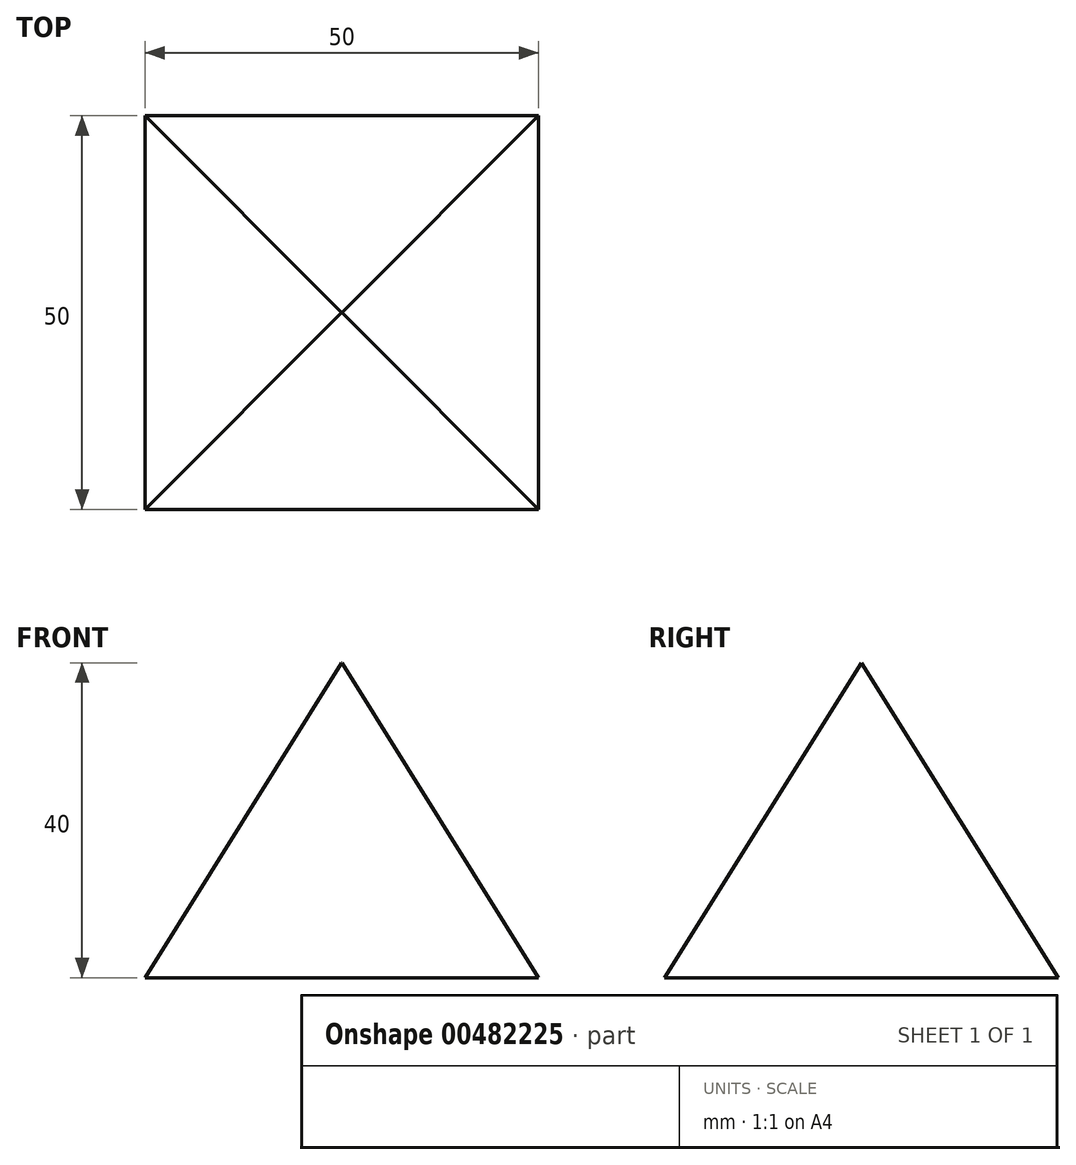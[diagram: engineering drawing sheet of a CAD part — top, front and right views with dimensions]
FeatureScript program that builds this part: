
annotation { "Feature Type Name" : "Feature", "Feature Type Description" : "" }
export const myFeature = defineFeature(function(context is Context, id is Id, definition is map)
    precondition{}
    {
        {
            var Q0;
            Q0=qCreatedBy(makeId("Top.planeOp"),FACE);
            var sketch = newSketch(context, id + "F0", { "sketchPlane" : qUnion([Q0])});
            skLineSegment(sketch, "E0.bottom", {"start": v(25, 25) * mm, "end": v(-25, 25) * mm});
            skLineSegment(sketch, "E0.top", {"start": v(25, -25) * mm, "end": v(-25, -25) * mm});
            skLineSegment(sketch, "E0.left", {"start": v(25, 25) * mm, "end": v(25, -25) * mm});
            skLineSegment(sketch, "E0.right", {"start": v(-25, 25) * mm, "end": v(-25, -25) * mm});
            skPoint(sketch, "E0.middle", {"position": v(0, 0) * mm});
            skSolve(sketch);
        }
        {
            var Q0;
            Q0 = qSketchRegion(id + "F0", true);
            extrude(context, id + "F1", {"entities" : qUnion([Q0]), "depth" : 40 * mm, "hasDraft" : true, "draftAngle" : 32 * degree, "draftPullDirection" : true});
        }
    });
